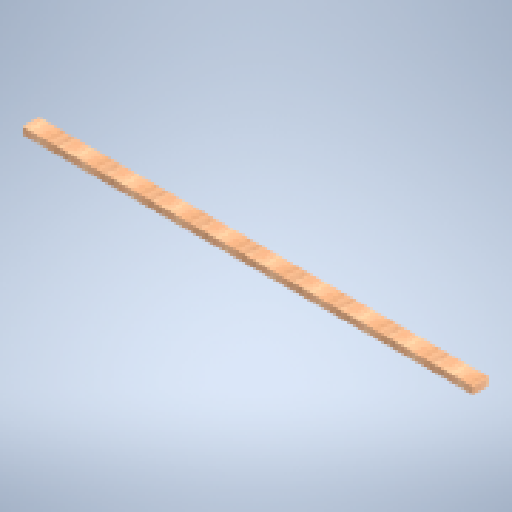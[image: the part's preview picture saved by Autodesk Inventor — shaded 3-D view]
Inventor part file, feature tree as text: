
AUTODESK INVENTOR PART (.ipt)
format: ipt  version: 2025 (Build 290162000, 162)  size: 150,528 bytes
history: native  units: in
note: dims shown in document units (in); Inventor stores cm internally (conversion verified against a paired STEP export)
features: extrude x1, move_body x1, sketch x1
ambient origin geometry x8: Origin, YZ Plane, XZ Plane, XY Plane, X Axis, Y Axis, Z Axis, Center Point
bodies: Solid1 (feature_tree)
feature tree (3):
  extrude  "Extrusion1"  Depth=3.5in
  move_body  "Move Body1"
  sketch  "Sketch1"  dims[d0=96.0in d1=3.5in d2=1.5in d3=0.0in d6=90.0deg]
